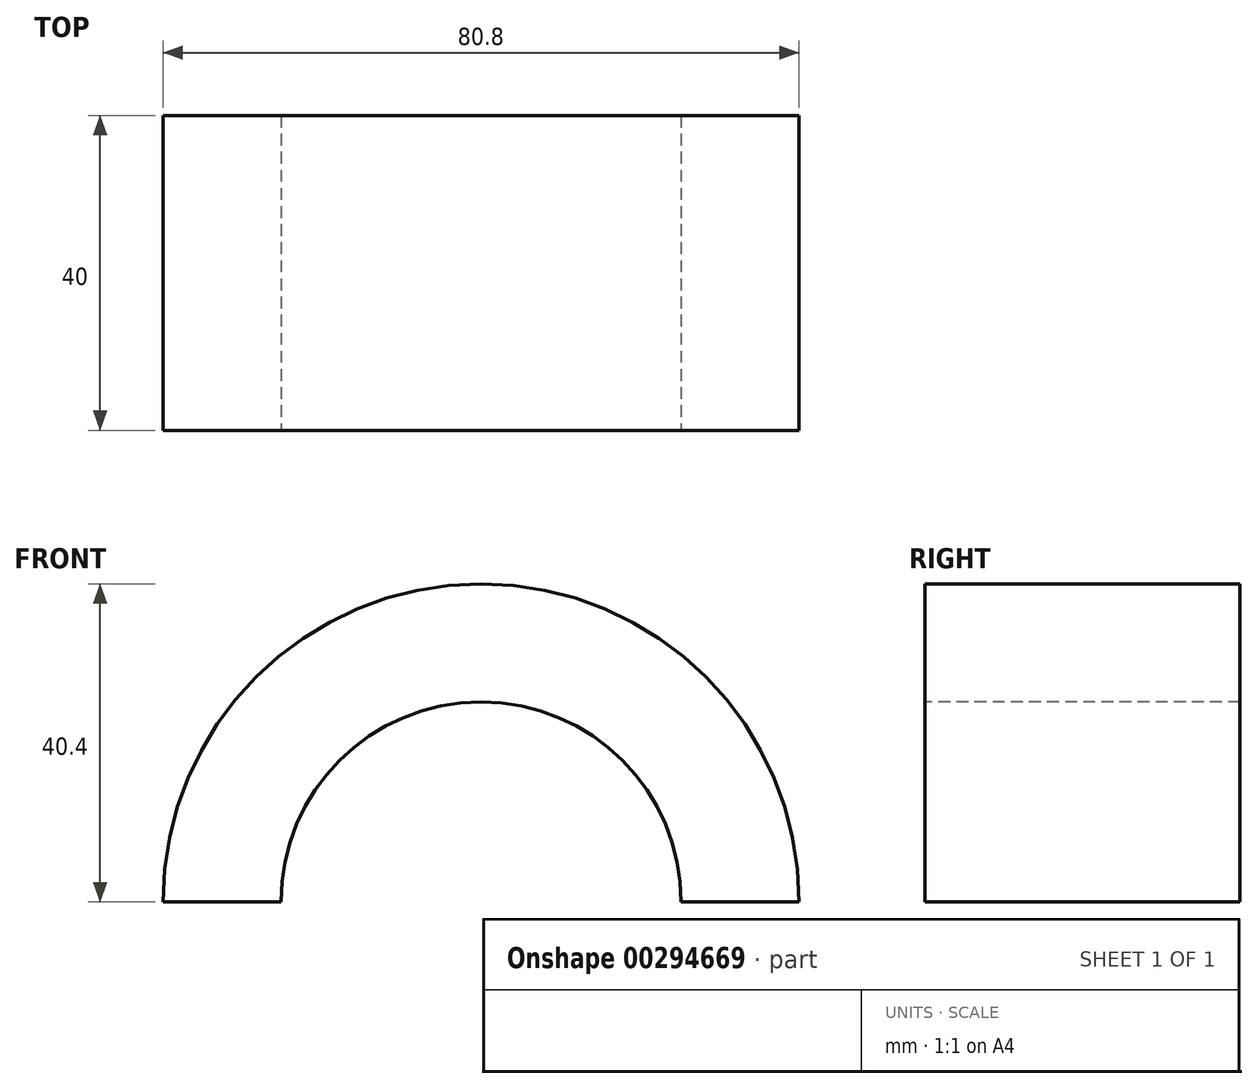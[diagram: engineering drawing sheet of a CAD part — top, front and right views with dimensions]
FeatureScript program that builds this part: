
annotation { "Feature Type Name" : "Feature", "Feature Type Description" : "" }
export const myFeature = defineFeature(function(context is Context, id is Id, definition is map)
    precondition{}
    {
        {
            var Q0;
            Q0=qCreatedBy(makeId("Front.planeOp"),FACE);
            var sketch = newSketch(context, id + "F0", { "sketchPlane" : qUnion([Q0])});
            skArc(sketch, "E0", {"start": v(40.4, 0) * mm, "mid": v(0, 40.4) * mm, "end": v(-40.4, 0) * mm});
            skLineSegment(sketch, "E1", {"start": v(40.4, 0) * mm, "end": v(-40.4, 0) * mm});
            skSolve(sketch);
        }
        {
            var Q0;
            Q0=makeQuery(id+"F0.imprint","IMPRINT",FACE,{"disambiguationData":[TD([[makeQuery(id+"F0.imprint","IMPRINT",EDGE,{"derivedFrom":sQuery(id+"F0.wireOp",EDGE,"E0")}),1.0]])]});
            extrude(context, id + "F1", {"entities" : qUnion([Q0]), "depth" : 40 * mm});
        }
        {
            var Q0;
            Q0=makeQuery(id+"F1.opExtrude","CAP_FACE",FACE,{"disambiguationData":[OSD([sQuery(id+"F0.wireOp",EDGE,"E0")])],"isStart":false});
            var sketch = newSketch(context, id + "F2", { "sketchPlane" : qUnion([Q0])});
            skCircle(sketch, "E2", {"center": v(0, 0) * mm, "radius": 25.4 * mm});
            skSolve(sketch);
        }
        {
            var Q0;
            Q0=makeQuery(id+"F2.imprint","IMPRINT",FACE,{"disambiguationData":[TD([[makeQuery(id+"F2.imprint","IMPRINT",EDGE,{"derivedFrom":sQuery(id+"F2.wireOp",EDGE,"E2")}),1.0]])]});
            extrude(context, id + "F3", {"entities" : qUnion([Q0]), "operationType" : NewBodyOperationType.REMOVE, "oppositeDirection" : true, "depth" : 40 * mm});
        }
    });
